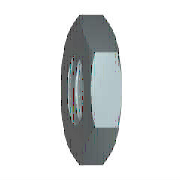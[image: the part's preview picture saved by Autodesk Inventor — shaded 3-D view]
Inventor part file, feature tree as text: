
AUTODESK INVENTOR PART (.ipt)
format: ipt  version: 2022 (Build 260153000, 153)  size: 164,352 bytes
history: native  units: mm (DEFAULTED — no unit token found)
features: sketch x3, extrude x1, chamfer x1, hole x1, other x1, plane x1
ambient origin geometry x7: Origin, YZ Plane, XZ Plane, X Axis, Y Axis, Z Axis, Center Point
bodies: Solid1 (feature_tree)
feature tree (8):
  extrude  "Cuerpo"  Depth=1.2mm
  chamfer  "Chaflán1"  Angle=30.0deg  [1 undecoded]
  hole  "Rosca"  [1 undecoded]
  other  "Work Axis1"
  plane  "Work Plane1"
  sketch  "Boceto1"  dims[d0=4.618802mm d1=1.2mm]
  sketch  "Boceto2"  dims[d2=0.0mm]
  sketch  "Boceto3"  dims[d3=30.0deg d4=30.0deg d5=3.1mm d6=3.1mm d7=90.0deg d25=1.567mm d26=6.0mm d27=4.0mm d28=2.0mm d29=14.3117mm d30=8.0mm d31=20.594885mm d8=0.216506mm d9=30.0deg d10=0.216506mm d11=30.0deg d13=0.0mm d14=0.0mm d39=0.0mm d40=0.216506mm d41=0.216506mm d42=0.0mm]
note: 2 required parameter values undecoded (feature->parameter linkage not recoverable at this tier; creation-order binding heuristic only, values carry confidence <= 0.55)
